# Revit family: 700_XO_Standard
name_source: partatom
category: Doors
revit_build: Autodesk Revit 2014 (Build: 20130308_1515(x64)
units: mm (PartAtom-declared; Revit-internal decimal feet)

## types (16) — shared parameters
Centered In Wall = Yes
Custom Door Height = 2090 mm  [stored 6.85696 ft]
Custom Sash Width Left = 600 mm
Description = Sliding door, XO
Equal Sash Width = Yes
Frame Thickness = 72 mm
Heavy Duty Interlocker = No
Height = 2090 mm  [stored 6.85696 ft]
Limit Door Height Max = 2142 mm
Limit Door Height Min = 342 mm
Limit Door Width Min = 612 mm
Limit Sash Height Max = 2100 mm
Limit Sash Height Min = 300 mm  [stored 0.984252 ft]
Limit Sash Width Max = 1500 mm
Limit Sash Width Min = 300 mm  [stored 0.984252 ft]
Manufacturer = Crealco
Model = Series 700
Rough Width = 3 mm  [stored 0.00984252 ft]
Sash Frame Seal = 2 mm  [stored 0.00656168 ft]
Sash Frame Side Gap = 10 mm  [stored 0.0328084 ft]
Sash Frame Top Gap = 16 mm  [stored 0.0524934 ft]
Sash Height = 2048 mm
Standard Interlocker = Yes
URL = http://www.crealco.co.za
Wall Closure = By host
zero-valued in all types: Custom Frame Offset From Exterior, Default Sill Height

## per-type parameters (varying)
| type | Area Left Sash Glazing | Area Right Sash Glazing | Custom Door Width | Custom Windload | Interlock Configuration | Intruderprufe LowE SHGC Value | Intruderprufe LowE U Value | Intruderprufe SHGC Value | Intruderprufe U Value | Limit Door Width Max | Limit Sash Width Left Max | Limit Sash Width Left Min | Max Pane Area | Sash Width Left | Sash Width Right | Toughened Safety SHGC Value | Toughened Safety U Value | Width | Windload Design |
| 700-1521XO-1000Pa | 1.31 m² | 1.35 m² | 1490 mm | 1000 mm  [stored 3.28084 ft] | 2 mm  [stored 0.00656168 ft] | 0.578 | 4.99 | 0.654 | 6.35 | 2990 mm  [stored 9.80971 ft] | 1178 mm | 300 mm  [stored 0.984252 ft] | 1.35 m² | 739 mm | 739 mm | 0.69 | 6.43 | 1490 mm | 1000 mm  [stored 3.28084 ft] |
| 700-1521XO-1500Pa | 1.31 m² | 1.35 m² | 1490 mm | 1500 mm | 3 mm  [stored 0.00984252 ft] | 0.578 | 4.99 | 0.654 | 6.35 | 2990 mm  [stored 9.80971 ft] | 1178 mm | 300 mm  [stored 0.984252 ft] | 1.35 m² | 739 mm | 739 mm | 0.69 | 6.43 | 1490 mm | 1500 mm |
| 700-1521XO-2000Pa | 1.31 m² | 1.35 m² | 1490 mm | 2000 mm  [stored 6.56168 ft] | 3 mm  [stored 0.00984252 ft] | 0.578 | 4.99 | 0.654 | 6.35 | 1790 mm | 1178 mm | 300 mm  [stored 0.984252 ft] | 1.35 m² | 739 mm | 739 mm | 0.69 | 6.43 | 1490 mm | 2000 mm  [stored 6.56168 ft] |
| 700-1821XO-1000Pa | 1.61 m² | 1.65 m² | 1790 mm | 1000 mm  [stored 3.28084 ft] | 2 mm  [stored 0.00656168 ft] | 0.59 | 4.83 | 0.669 | 6.26 | 2990 mm  [stored 9.80971 ft] | 1478 mm | 300 mm  [stored 0.984252 ft] | 1.65 m² | 889 mm | 889 mm | 0.706 | 6.35 | 1790 mm | 1000 mm  [stored 3.28084 ft] |
| 700-1821XO-1500Pa | 1.61 m² | 1.65 m² | 1790 mm | 1500 mm | 3 mm  [stored 0.00984252 ft] | 0.59 | 4.83 | 0.669 | 6.26 | 2990 mm  [stored 9.80971 ft] | 1478 mm | 300 mm  [stored 0.984252 ft] | 1.65 m² | 889 mm | 889 mm | 0.706 | 6.35 | 1790 mm | 1500 mm |
| 700-1821XO-2000Pa | 1.61 m² | 1.65 m² | 1790 mm | 2000 mm  [stored 6.56168 ft] | 3 mm  [stored 0.00984252 ft] | 0.59 | 4.83 | 0.669 | 6.26 | 1790 mm | 1478 mm | 300 mm  [stored 0.984252 ft] | 1.65 m² | 889 mm | 889 mm | 0.706 | 6.35 | 1790 mm | 2000 mm  [stored 6.56168 ft] |
| 700-2021XO-1000Pa | 1.8 m² | 1.84 m² | 1990 mm  [stored 6.52887 ft] | 1000 mm  [stored 3.28084 ft] | 2 mm  [stored 0.00656168 ft] | 0.597 | 4.75 | 0.677 | 6.22 | 2990 mm  [stored 9.80971 ft] | 1500 mm | 478 mm | 1.84 m² | 989 mm | 989 mm | 0.714 | 6.31 | 1990 mm  [stored 6.52887 ft] | 1000 mm  [stored 3.28084 ft] |
| 700-2021XO-1500Pa | 1.8 m² | 1.84 m² | 1990 mm  [stored 6.52887 ft] | 1500 mm | 3 mm  [stored 0.00984252 ft] | 0.597 | 4.75 | 0.677 | 6.22 | 2990 mm  [stored 9.80971 ft] | 1500 mm | 478 mm | 1.84 m² | 989 mm | 989 mm | 0.714 | 6.31 | 1990 mm  [stored 6.52887 ft] | 1500 mm |
| 700-2121XO-1000Pa | 1.9 m² | 1.94 m² | 2090 mm  [stored 6.85696 ft] | 1000 mm  [stored 3.28084 ft] | 3 mm  [stored 0.00984252 ft] | 0.6 | 4.72 | 0.68 | 6.21 | 2990 mm  [stored 9.80971 ft] | 1500 mm | 578 mm | 1.94 m² | 1039 mm | 1039 mm | 0.717 | 6.3 | 2090 mm  [stored 6.85696 ft] | 1000 mm  [stored 3.28084 ft] |
| 700-2121XO-1500Pa | 1.9 m² | 1.94 m² | 2090 mm  [stored 6.85696 ft] | 1500 mm | 3 mm  [stored 0.00984252 ft] | 0.6 | 4.72 | 0.68 | 6.21 | 2990 mm  [stored 9.80971 ft] | 1500 mm | 578 mm | 1.94 m² | 1039 mm | 1039 mm | 0.717 | 6.3 | 2090 mm  [stored 6.85696 ft] | 1500 mm |
| 700-2421XO-1000Pa | 2.2 m² | 2.24 m² | 2390 mm | 1000 mm  [stored 3.28084 ft] | 3 mm  [stored 0.00984252 ft] | 0.607 | 4.63 | 0.688 | 6.16 | 2990 mm  [stored 9.80971 ft] | 1500 mm | 878 mm | 2.24 m² | 1189 mm | 1189 mm | 0.726 | 6.26 | 2390 mm | 1000 mm  [stored 3.28084 ft] |
| 700-2421XO-1500Pa | 2.2 m² | 2.24 m² | 2390 mm | 1500 mm | 3 mm  [stored 0.00984252 ft] | 0.607 | 4.63 | 0.688 | 6.16 | 2990 mm  [stored 9.80971 ft] | 1500 mm | 878 mm | 2.24 m² | 1189 mm | 1189 mm | 0.726 | 6.26 | 2390 mm | 1500 mm |
| 700-2721XO-1000Pa | 2.49 m² | 2.53 m² | 2690 mm | 1000 mm  [stored 3.28084 ft] | 3 mm  [stored 0.00984252 ft] | 0.612 | 4.56 | 0.694 | 6.13 | 2990 mm  [stored 9.80971 ft] | 1500 mm | 1178 mm | 2.53 m² | 1339 mm | 1339 mm | 0.732 | 6.22 | 2690 mm | 1000 mm  [stored 3.28084 ft] |
| 700-2721XO-1500Pa | 2.49 m² | 2.53 m² | 2690 mm | 1500 mm | 3 mm  [stored 0.00984252 ft] | 0.612 | 4.56 | 0.694 | 6.13 | 2990 mm  [stored 9.80971 ft] | 1500 mm | 1178 mm | 2.53 m² | 1339 mm | 1339 mm | 0.732 | 6.22 | 2690 mm | 1500 mm |
| 700-3021XO-1000Pa | 2.79 m² | 2.83 m² | 2990 mm  [stored 9.80971 ft] | 1000 mm  [stored 3.28084 ft] | 3 mm  [stored 0.00984252 ft] | 0.616 | 4.51 | 0.699 | 6.1 | 2990 mm  [stored 9.80971 ft] | 1500 mm | 1478 mm | 2.83 m² | 1489 mm | 1489 mm | 0.738 | 6.2 | 2990 mm  [stored 9.80971 ft] | 1000 mm  [stored 3.28084 ft] |
| 700-3021XO-1500Pa | 2.79 m² | 2.83 m² | 2990 mm  [stored 9.80971 ft] | 1500 mm | 3 mm  [stored 0.00984252 ft] | 0.616 | 4.51 | 0.699 | 6.1 | 2990 mm  [stored 9.80971 ft] | 1500 mm | 1478 mm | 2.83 m² | 1489 mm | 1489 mm | 0.738 | 6.2 | 2990 mm  [stored 9.80971 ft] | 1500 mm |

note: [stored X ft] marks values corroborated as IEEE doubles in the binary element streams (Revit-internal decimal feet)

## geometry (parser evidence)
native form markers: Sweep x50
no freeform markers — native parametric forms only
